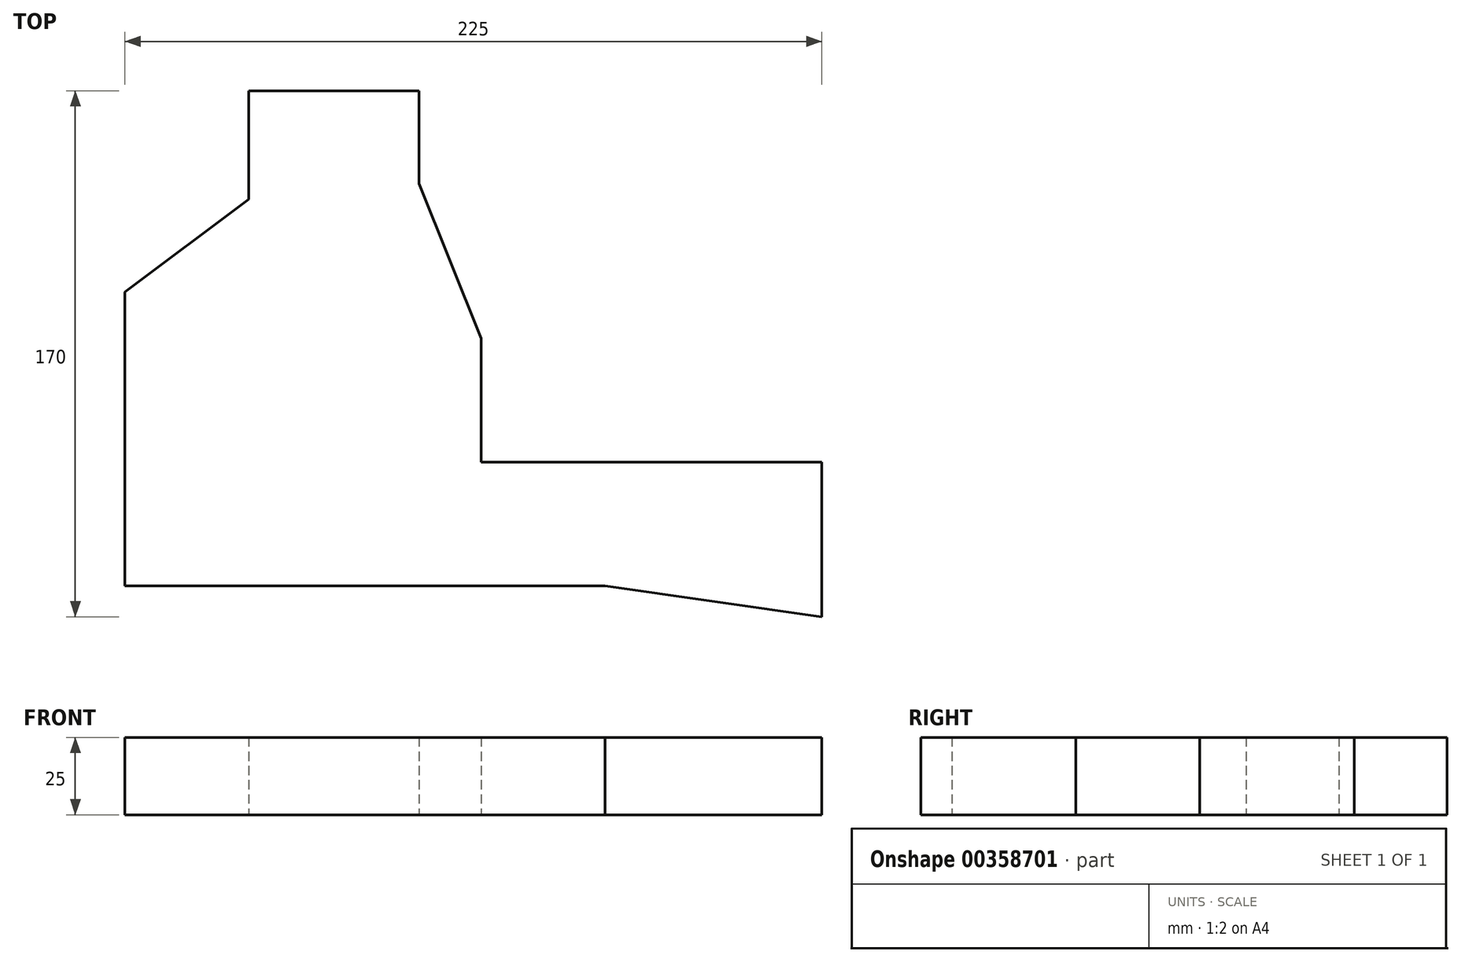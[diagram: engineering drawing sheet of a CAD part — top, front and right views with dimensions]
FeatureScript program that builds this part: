
annotation { "Feature Type Name" : "Feature", "Feature Type Description" : "" }
export const myFeature = defineFeature(function(context is Context, id is Id, definition is map)
    precondition{}
    {
        {
            var Q0;
            Q0=qCreatedBy(makeId("Top.planeOp"),FACE);
            var sketch = newSketch(context, id + "F0", { "sketchPlane" : qUnion([Q0])});
            skLineSegment(sketch, "E0", {"start": v(-55.34, -60.2) * mm, "end": v(-55.34, 34.8) * mm});
            skLineSegment(sketch, "E1", {"start": v(-15.34, 64.8) * mm, "end": v(-55.34, 34.8) * mm});
            skLineSegment(sketch, "E2", {"start": v(-15.34, 64.8) * mm, "end": v(-15.34, 99.8) * mm});
            skLineSegment(sketch, "E3", {"start": v(-15.34, 99.8) * mm, "end": v(39.66, 99.8) * mm});
            skLineSegment(sketch, "E4", {"start": v(39.66, 99.8) * mm, "end": v(39.66, 69.8) * mm});
            skLineSegment(sketch, "E5", {"start": v(59.66, 19.8) * mm, "end": v(39.66, 69.8) * mm});
            skLineSegment(sketch, "E6", {"start": v(59.66, 19.8) * mm, "end": v(59.66, -20.2) * mm});
            skLineSegment(sketch, "E7", {"start": v(169.66, -20.2) * mm, "end": v(59.66, -20.2) * mm});
            skLineSegment(sketch, "E8", {"start": v(169.66, -20.2) * mm, "end": v(169.66, -70.2) * mm});
            skLineSegment(sketch, "E9", {"start": v(99.66, -60.2) * mm, "end": v(169.66, -70.2) * mm});
            skLineSegment(sketch, "E10", {"start": v(-55.34, -60.2) * mm, "end": v(99.66, -60.2) * mm});
            skPoint(sketch, "E11.orphan", {"position": v(99.66, 99.8) * mm});
            skPoint(sketch, "E12.end.orphan", {"position": v(99.66, -70.2) * mm});
            skSolve(sketch);
        }
        {
            var Q0;
            Q0=makeQuery(id+"F0.imprint","IMPRINT",FACE,{"disambiguationData":[TD([[makeQuery(id+"F0.imprint","IMPRINT",EDGE,{"derivedFrom":sQuery(id+"F0.wireOp",EDGE,"E0")}),-1.0]])]});
            extrude(context, id + "F1", {"entities" : qUnion([Q0]), "depth" : 25 * mm});
        }
    });
